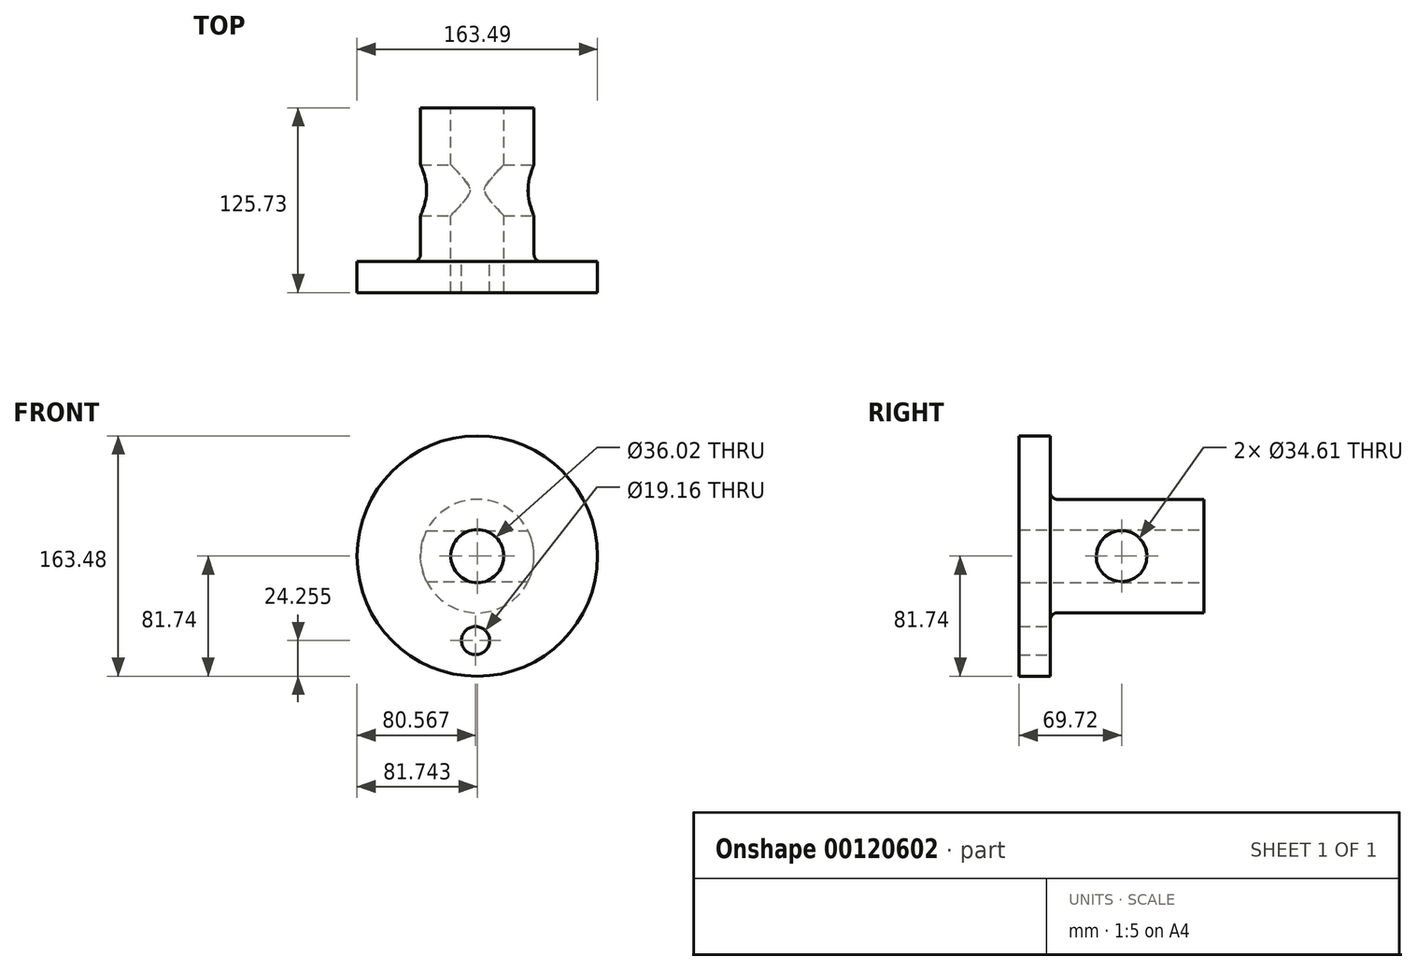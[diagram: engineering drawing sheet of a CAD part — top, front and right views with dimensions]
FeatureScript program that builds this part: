
annotation { "Feature Type Name" : "Feature", "Feature Type Description" : "" }
export const myFeature = defineFeature(function(context is Context, id is Id, definition is map)
    precondition{}
    {
        {
            var Q0;
            Q0=qCreatedBy(makeId("Top.planeOp"),FACE);
            var sketch = newSketch(context, id + "F0", { "sketchPlane" : qUnion([Q0])});
            skLineSegment(sketch, "E0.bottom", {"start": v(-55.87, 56.01) * mm, "end": v(-35.28, 56.01) * mm});
            skLineSegment(sketch, "E0.left", {"start": v(-55.87, 56.01) * mm, "end": v(-55.87, -48.66) * mm});
            skLineSegment(sketch, "E0.right", {"start": v(-35.28, 56.01) * mm, "end": v(-35.28, -48.66) * mm});
            skLineSegment(sketch, "E1.bottom", {"start": v(-55.87, -48.66) * mm, "end": v(-99.02, -48.66) * mm});
            skLineSegment(sketch, "E1.top", {"start": v(-35.28, -69.72) * mm, "end": v(-99.02, -69.72) * mm});
            skLineSegment(sketch, "E1.left", {"start": v(-35.28, -48.66) * mm, "end": v(-35.28, -69.72) * mm});
            skLineSegment(sketch, "E1.right", {"start": v(-99.02, -48.66) * mm, "end": v(-99.02, -69.72) * mm});
            skLineSegment(sketch, "E2", {"start": v(-17.28, 81.7) * mm, "end": v(-17.28, -95.3) * mm});
            skSolve(sketch);
        }
        {
            var Q0;
            Q0=makeQuery(id+"F0.imprint","IMPRINT",FACE,{"disambiguationData":[TD([[makeQuery(id+"F0.imprint","IMPRINT",EDGE,{"derivedFrom":sQuery(id+"F0.wireOp",EDGE,"E0.bottom")}),-1.0]])]});
            var Q1;
            Q1=sQuery(id+"F0.wireOp",EDGE,"E2");
            revolve(context, id + "F1", {"entities" : qUnion([Q0]), "axis" : qUnion([Q1]), "revolveType" : RevolveType.FULL});
        }
        {
            var Q0;
            Q0=makeQuery(id+"F1.opRevolve","SWEPT_FACE",FACE,{"disambiguationData":[OSD([sQuery(id+"F0.wireOp",EDGE,"E1.bottom")])]});
            var sketch = newSketch(context, id + "F2", { "sketchPlane" : qUnion([Q0])});
            skCircle(sketch, "E3", {"center": v(18.45, -57.49) * mm, "radius": 9.58 * mm});
            skSolve(sketch);
        }
        {
            var Q0;
            Q0=makeQuery(id+"F2.imprint","IMPRINT",FACE,{"disambiguationData":[TD([[makeQuery(id+"F2.imprint","IMPRINT",EDGE,{"derivedFrom":sQuery(id+"F2.wireOp",EDGE,"E3")}),1.0]])]});
            extrude(context, id + "F3", {"entities" : qUnion([Q0]), "operationType" : NewBodyOperationType.REMOVE, "oppositeDirection" : true, "depth" : 25.4 * mm});
        }
        {
            var Q0;
            Q0=makeQuery(id+"F1.opRevolve","SWEPT_EDGE",EDGE,{"disambiguationData":[OSD([sQuery(id+"F0.wireOp",EDGE,"E0.left"),sQuery(id+"F0.wireOp",EDGE,"E1.bottom")])]});
            fillet(context, id + "F4", {"entities" : qUnion([Q0]), "radius" : 5.08 * mm, "tangentPropagation" : true, "allowEdgeOverflow" : false});
        }
        {
            var Q0;
            Q0=qCreatedBy(makeId("Right.planeOp"),FACE);
            var sketch = newSketch(context, id + "F5", { "sketchPlane" : qUnion([Q0])});
            skCircle(sketch, "E4", {"center": v(0, 0) * mm, "radius": 17.3 * mm});
            skSolve(sketch);
        }
        {
            var Q0;
            Q0=makeQuery(id+"F5.imprint","IMPRINT",FACE,{"disambiguationData":[TD([[makeQuery(id+"F5.imprint","IMPRINT",EDGE,{"derivedFrom":sQuery(id+"F5.wireOp",EDGE,"E4")}),1.0]])]});
            extrude(context, id + "F6", {"entities" : qUnion([Q0]), "operationType" : NewBodyOperationType.REMOVE, "endBound" : BoundingType.SYMMETRIC, "oppositeDirection" : true, "depth" : 140.2 * mm, "offsetDistance" : 25.4 * mm});
        }
    });
